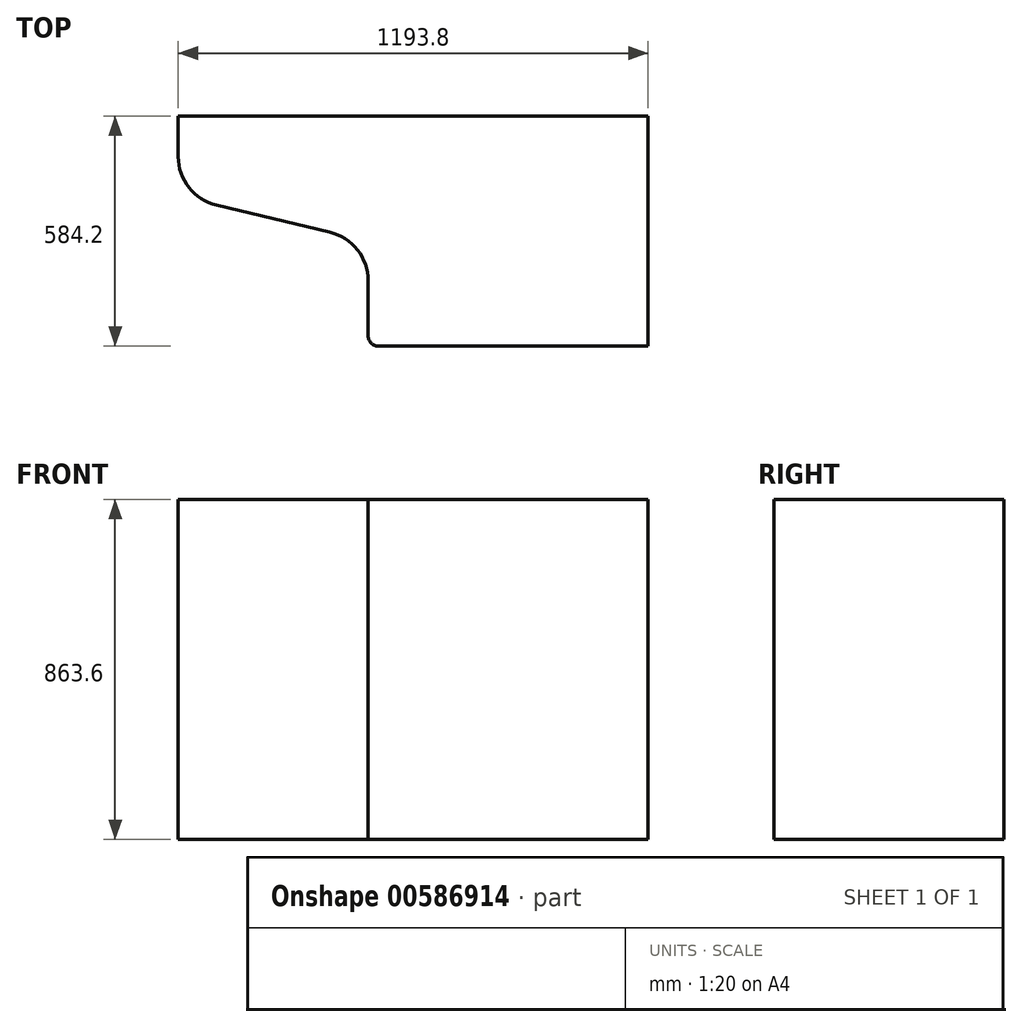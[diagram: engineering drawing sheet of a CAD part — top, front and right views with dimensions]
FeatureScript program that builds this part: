
annotation { "Feature Type Name" : "Feature", "Feature Type Description" : "" }
export const myFeature = defineFeature(function(context is Context, id is Id, definition is map)
    precondition{}
    {
        {
            var Q0;
            Q0=qCreatedBy(makeId("Top.planeOp"),FACE);
            var sketch = newSketch(context, id + "F0", { "sketchPlane" : qUnion([Q0])});
            skLineSegment(sketch, "E0.bottom", {"start": v(0, 0) * mm, "end": v(-1193.8, 0) * mm});
            skLineSegment(sketch, "E0.top", {"start": v(0, -584.2) * mm, "end": v(-685.8, -584.2) * mm});
            skLineSegment(sketch, "E0.left", {"start": v(0, 0) * mm, "end": v(0, -584.2) * mm});
            skLineSegment(sketch, "E0.right", {"start": v(-1193.8, 0) * mm, "end": v(-1193.8, -102.91) * mm});
            skLineSegment(sketch, "E1.top", {"start": v(-1096.24, -226.45) * mm, "end": v(-808.76, -294.97) * mm});
            skLineSegment(sketch, "E1.right", {"start": v(-711.2, -558.8) * mm, "end": v(-711.2, -418.5) * mm});
            skPoint(sketch, "E2.visualSharp", {"position": v(-711.2, -318.22) * mm});
            skArc(sketch, "E2.filletArc", {"start": v(-711.2, -418.5) * mm, "mid": v(-740.47, -337.4) * mm, "end": v(-814.8, -293.68) * mm});
            skPoint(sketch, "E3.visualSharp", {"position": v(-1193.8, -203.2) * mm});
            skArc(sketch, "E3.filletArc", {"start": v(-1193.8, -102.91) * mm, "mid": v(-1166.47, -181.62) * mm, "end": v(-1096.24, -226.45) * mm});
            skPoint(sketch, "E4.visualSharp", {"position": v(-808.76, -294.97) * mm});
            skArc(sketch, "E4.filletArc", {"start": v(-711.2, -418.5) * mm, "mid": v(-738.53, -339.8) * mm, "end": v(-808.76, -294.97) * mm});
            skPoint(sketch, "E5.visualSharp", {"position": v(-711.2, -584.2) * mm});
            skArc(sketch, "E5.filletArc", {"start": v(-711.2, -558.8) * mm, "mid": v(-703.76, -576.76) * mm, "end": v(-685.8, -584.2) * mm});
            skSolve(sketch);
        }
        {
            var Q0;
            Q0=makeQuery(id+"F0.imprint","IMPRINT",FACE,{"disambiguationData":[TD([[makeQuery(id+"F0.imprint","IMPRINT",EDGE,{"derivedFrom":sQuery(id+"F0.wireOp",EDGE,"E0.bottom")}),1.0]])]});
            extrude(context, id + "F1", {"entities" : qUnion([Q0]), "depth" : 863.6 * mm, "offsetDistance" : 25.4 * mm});
        }
    });
